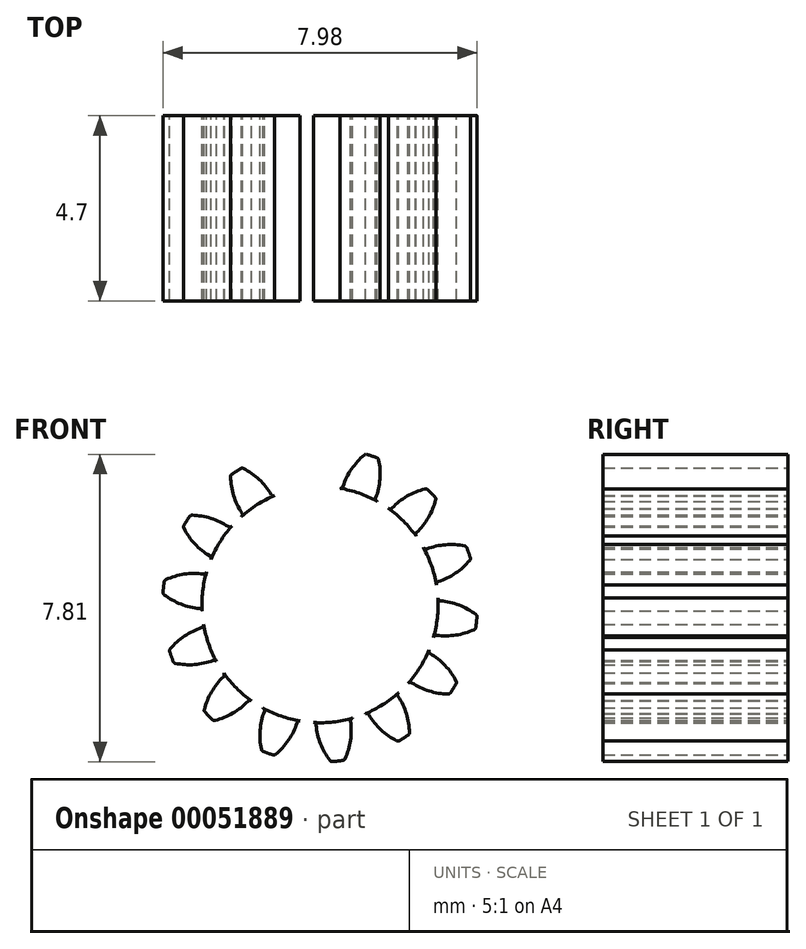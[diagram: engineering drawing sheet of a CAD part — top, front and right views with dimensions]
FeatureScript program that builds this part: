
annotation { "Feature Type Name" : "Feature", "Feature Type Description" : "" }
export const myFeature = defineFeature(function(context is Context, id is Id, definition is map)
    precondition{}
    {
        {
            var Q0;
            Q0=qCreatedBy(makeId("Front.planeOp"),FACE);
            var sketch = newSketch(context, id + "F0", { "sketchPlane" : qUnion([Q0])});
            skCircle(sketch, "E0", {"center": v(0, 0) * mm, "radius": 3 * mm, "construction": true});
            skCircle(sketch, "E1", {"center": v(0, 0) * mm, "radius": 3.5 * mm, "construction": true});
            skCircle(sketch, "E2", {"center": v(0, 0) * mm, "radius": 4 * mm, "construction": true});
            skLineSegment(sketch, "E3", {"start": v(0, 8.23) * mm, "end": v(0, 0) * mm, "construction": true});
            skCircle(sketch, "E4.cCircle", {"center": v(0, 0) * mm, "radius": 8.23 * mm, "construction": true});
            skLineSegment(sketch, "E4.0", {"start": v(0, 8.23) * mm, "end": v(1.83, 8.03) * mm, "construction": true});
            skLineSegment(sketch, "E4.1", {"start": v(1.83, 8.03) * mm, "end": v(3.57, 7.42) * mm, "construction": true});
            skLineSegment(sketch, "E4.2", {"start": v(3.57, 7.42) * mm, "end": v(5.13, 6.44) * mm, "construction": true});
            skLineSegment(sketch, "E4.3", {"start": v(5.13, 6.44) * mm, "end": v(6.44, 5.13) * mm, "construction": true});
            skLineSegment(sketch, "E4.4", {"start": v(6.44, 5.13) * mm, "end": v(7.42, 3.57) * mm, "construction": true});
            skLineSegment(sketch, "E4.5", {"start": v(7.42, 3.57) * mm, "end": v(8.03, 1.83) * mm, "construction": true});
            skLineSegment(sketch, "E4.6", {"start": v(8.03, 1.83) * mm, "end": v(8.23, 0) * mm, "construction": true});
            skLineSegment(sketch, "E4.7", {"start": v(8.23, 0) * mm, "end": v(8.03, -1.83) * mm, "construction": true});
            skLineSegment(sketch, "E4.8", {"start": v(8.03, -1.83) * mm, "end": v(7.42, -3.57) * mm, "construction": true});
            skLineSegment(sketch, "E4.9", {"start": v(7.42, -3.57) * mm, "end": v(6.44, -5.13) * mm, "construction": true});
            skLineSegment(sketch, "E4.10", {"start": v(6.44, -5.13) * mm, "end": v(5.13, -6.44) * mm, "construction": true});
            skLineSegment(sketch, "E4.11", {"start": v(5.13, -6.44) * mm, "end": v(3.57, -7.42) * mm, "construction": true});
            skLineSegment(sketch, "E4.12", {"start": v(3.57, -7.42) * mm, "end": v(1.83, -8.03) * mm, "construction": true});
            skLineSegment(sketch, "E4.13", {"start": v(1.83, -8.03) * mm, "end": v(0, -8.23) * mm, "construction": true});
            skLineSegment(sketch, "E4.14", {"start": v(0, -8.23) * mm, "end": v(-1.83, -8.03) * mm, "construction": true});
            skLineSegment(sketch, "E4.15", {"start": v(-1.83, -8.03) * mm, "end": v(-3.57, -7.42) * mm, "construction": true});
            skLineSegment(sketch, "E4.16", {"start": v(-3.57, -7.42) * mm, "end": v(-5.13, -6.44) * mm, "construction": true});
            skLineSegment(sketch, "E4.17", {"start": v(-5.13, -6.44) * mm, "end": v(-6.44, -5.13) * mm, "construction": true});
            skLineSegment(sketch, "E4.18", {"start": v(-6.44, -5.13) * mm, "end": v(-7.42, -3.57) * mm, "construction": true});
            skLineSegment(sketch, "E4.19", {"start": v(-7.42, -3.57) * mm, "end": v(-8.03, -1.83) * mm, "construction": true});
            skLineSegment(sketch, "E4.20", {"start": v(-8.03, -1.83) * mm, "end": v(-8.23, 0) * mm, "construction": true});
            skLineSegment(sketch, "E4.21", {"start": v(-8.23, 0) * mm, "end": v(-8.03, 1.83) * mm, "construction": true});
            skLineSegment(sketch, "E4.22", {"start": v(-8.03, 1.83) * mm, "end": v(-7.42, 3.57) * mm, "construction": true});
            skLineSegment(sketch, "E4.23", {"start": v(-7.42, 3.57) * mm, "end": v(-6.44, 5.13) * mm, "construction": true});
            skLineSegment(sketch, "E4.24", {"start": v(-6.44, 5.13) * mm, "end": v(-5.13, 6.44) * mm, "construction": true});
            skLineSegment(sketch, "E4.25", {"start": v(-5.13, 6.44) * mm, "end": v(-3.57, 7.42) * mm, "construction": true});
            skLineSegment(sketch, "E4.26", {"start": v(-3.57, 7.42) * mm, "end": v(-1.83, 8.03) * mm, "construction": true});
            skLineSegment(sketch, "E4.27", {"start": v(-1.83, 8.03) * mm, "end": v(0, 8.23) * mm, "construction": true});
            skLineSegment(sketch, "E5.0", {"start": v(-0.93, 8.23) * mm, "end": v(0.93, 8.23) * mm, "construction": true});
            skLineSegment(sketch, "E5.1", {"start": v(0.93, 8.23) * mm, "end": v(2.74, 7.82) * mm, "construction": true});
            skLineSegment(sketch, "E5.2", {"start": v(2.74, 7.82) * mm, "end": v(4.4, 7.02) * mm, "construction": true});
            skLineSegment(sketch, "E5.3", {"start": v(4.4, 7.02) * mm, "end": v(5.86, 5.86) * mm});
            skLineSegment(sketch, "E5.4", {"start": v(5.86, 5.86) * mm, "end": v(7.02, 4.4) * mm});
            skLineSegment(sketch, "E5.5", {"start": v(7.02, 4.4) * mm, "end": v(7.82, 2.74) * mm});
            skLineSegment(sketch, "E5.6", {"start": v(7.82, 2.74) * mm, "end": v(8.23, 0.93) * mm});
            skLineSegment(sketch, "E5.7", {"start": v(8.23, 0.93) * mm, "end": v(8.23, -0.93) * mm});
            skLineSegment(sketch, "E5.8", {"start": v(8.23, -0.93) * mm, "end": v(7.82, -2.74) * mm});
            skLineSegment(sketch, "E5.9", {"start": v(7.82, -2.74) * mm, "end": v(7.02, -4.4) * mm});
            skLineSegment(sketch, "E5.10", {"start": v(7.02, -4.4) * mm, "end": v(5.86, -5.86) * mm});
            skLineSegment(sketch, "E5.11", {"start": v(5.86, -5.86) * mm, "end": v(4.4, -7.02) * mm});
            skLineSegment(sketch, "E5.12", {"start": v(4.4, -7.02) * mm, "end": v(2.74, -7.82) * mm});
            skLineSegment(sketch, "E5.13", {"start": v(2.74, -7.82) * mm, "end": v(0.93, -8.23) * mm});
            skLineSegment(sketch, "E5.14", {"start": v(0.93, -8.23) * mm, "end": v(-0.93, -8.23) * mm});
            skLineSegment(sketch, "E5.15", {"start": v(-0.93, -8.23) * mm, "end": v(-2.74, -7.82) * mm});
            skLineSegment(sketch, "E5.16", {"start": v(-2.74, -7.82) * mm, "end": v(-4.4, -7.02) * mm});
            skLineSegment(sketch, "E5.17", {"start": v(-4.4, -7.02) * mm, "end": v(-5.86, -5.86) * mm});
            skLineSegment(sketch, "E5.18", {"start": v(-5.86, -5.86) * mm, "end": v(-7.02, -4.4) * mm});
            skLineSegment(sketch, "E5.19", {"start": v(-7.02, -4.4) * mm, "end": v(-7.82, -2.74) * mm});
            skLineSegment(sketch, "E5.20", {"start": v(-7.82, -2.74) * mm, "end": v(-8.23, -0.93) * mm});
            skLineSegment(sketch, "E5.21", {"start": v(-8.23, -0.93) * mm, "end": v(-8.23, 0.93) * mm});
            skLineSegment(sketch, "E5.22", {"start": v(-8.23, 0.93) * mm, "end": v(-7.82, 2.74) * mm});
            skLineSegment(sketch, "E5.23", {"start": v(-7.82, 2.74) * mm, "end": v(-7.02, 4.4) * mm});
            skLineSegment(sketch, "E5.24", {"start": v(-7.02, 4.4) * mm, "end": v(-5.86, 5.86) * mm});
            skLineSegment(sketch, "E5.25", {"start": v(-5.86, 5.86) * mm, "end": v(-4.4, 7.02) * mm, "construction": true});
            skLineSegment(sketch, "E5.26", {"start": v(-4.4, 7.02) * mm, "end": v(-2.74, 7.82) * mm, "construction": true});
            skLineSegment(sketch, "E5.27", {"start": v(-2.74, 7.82) * mm, "end": v(-0.93, 8.23) * mm, "construction": true});
            skPoint(sketch, "E5.0.midPoint", {"position": v(0, 8.23) * mm});
            skLineSegment(sketch, "E6", {"start": v(-0.93, 8.23) * mm, "end": v(0, 0) * mm, "construction": true});
            skLineSegment(sketch, "E7", {"start": v(0, 3.5) * mm, "end": v(-9.32, 3.5) * mm, "construction": true});
            skLineSegment(sketch, "E8", {"start": v(0, 3.5) * mm, "end": v(-9.62, 0) * mm, "construction": true});
            skCircle(sketch, "E9", {"center": v(0, 3.5) * mm, "radius": 1.75 * mm, "construction": true});
            skCircle(sketch, "E10", {"center": v(-1.64, 2.9) * mm, "radius": 1.75 * mm, "construction": true});
            skArc(sketch, "E11", {"start": v(-0.25, 3.96) * mm, "mid": v(-0.01, 3.53) * mm, "end": v(0.1, 3.06) * mm});
            skArc(sketch, "E12.MirrorCS", {"start": v(-0.62, 3.95) * mm, "mid": v(-0.78, 3.44) * mm, "end": v(-0.77, 2.9) * mm});
            skArc(sketch, "E13.MirrorCS", {"start": v(-0.64, 3.92) * mm, "mid": v(-0.77, 3.45) * mm, "end": v(-0.78, 2.96) * mm});
            skArc(sketch, "E14", {"start": v(-0.58, 3.96) * mm, "mid": v(-0.45, 3.97) * mm, "end": v(-0.31, 3.99) * mm});
            skArc(sketch, "E15", {"start": v(-0.83, 2.88) * mm, "mid": v(0.34, -2.98) * mm, "end": v(0.16, 3) * mm});
            skPoint(sketch, "E16.visualSharp", {"position": v(-0.77, 2.9) * mm});
            skArc(sketch, "E16.filletArc", {"start": v(-0.83, 2.88) * mm, "mid": v(-0.79, 2.91) * mm, "end": v(-0.78, 2.96) * mm});
            skPoint(sketch, "E17.visualSharp", {"position": v(0.1, 3) * mm});
            skArc(sketch, "E17.filletArc", {"start": v(0.1, 3.06) * mm, "mid": v(0.12, 3.02) * mm, "end": v(0.16, 3) * mm});
            skPoint(sketch, "E18.visualSharp", {"position": v(-0.62, 3.95) * mm});
            skArc(sketch, "E18.filletArc", {"start": v(-0.58, 3.96) * mm, "mid": v(-0.61, 3.94) * mm, "end": v(-0.64, 3.92) * mm});
            skPoint(sketch, "E19.visualSharp", {"position": v(-0.27, 4) * mm});
            skArc(sketch, "E19.filletArc", {"start": v(-0.25, 3.96) * mm, "mid": v(-0.28, 3.98) * mm, "end": v(-0.31, 3.99) * mm});
            skArc(sketch, "E20.1.0", {"start": v(-2.27, 3.25) * mm, "mid": v(-2.2, 2.77) * mm, "end": v(-1.98, 2.33) * mm});
            skArc(sketch, "E20.1.1", {"start": v(-2, 2.24) * mm, "mid": v(-1.97, 2.28) * mm, "end": v(-1.98, 2.33) * mm});
            skArc(sketch, "E20.1.2", {"start": v(-2.24, 3.31) * mm, "mid": v(-2.27, 3.29) * mm, "end": v(-2.27, 3.25) * mm});
            skArc(sketch, "E20.1.3", {"start": v(-2.24, 3.31) * mm, "mid": v(-2.13, 3.39) * mm, "end": v(-2.01, 3.46) * mm});
            skArc(sketch, "E20.1.4", {"start": v(-1.94, 3.46) * mm, "mid": v(-1.55, 3.18) * mm, "end": v(-1.24, 2.8) * mm});
            skArc(sketch, "E20.1.5", {"start": v(-1.94, 3.46) * mm, "mid": v(-1.98, 3.47) * mm, "end": v(-2.01, 3.46) * mm});
            skArc(sketch, "E20.1.6", {"start": v(-1.24, 2.8) * mm, "mid": v(-1.2, 2.77) * mm, "end": v(-1.15, 2.77) * mm});
            skArc(sketch, "E20.2.0", {"start": v(-3.46, 1.94) * mm, "mid": v(-3.18, 1.55) * mm, "end": v(-2.8, 1.24) * mm});
            skArc(sketch, "E20.2.1", {"start": v(-2.77, 1.15) * mm, "mid": v(-2.77, 1.2) * mm, "end": v(-2.8, 1.24) * mm});
            skArc(sketch, "E20.2.2", {"start": v(-3.46, 2.01) * mm, "mid": v(-3.47, 1.98) * mm, "end": v(-3.46, 1.94) * mm});
            skArc(sketch, "E20.2.3", {"start": v(-3.46, 2.01) * mm, "mid": v(-3.39, 2.13) * mm, "end": v(-3.31, 2.24) * mm});
            skArc(sketch, "E20.2.4", {"start": v(-3.25, 2.27) * mm, "mid": v(-2.77, 2.2) * mm, "end": v(-2.33, 1.98) * mm});
            skArc(sketch, "E20.2.5", {"start": v(-3.25, 2.27) * mm, "mid": v(-3.29, 2.27) * mm, "end": v(-3.31, 2.24) * mm});
            skArc(sketch, "E20.2.6", {"start": v(-2.33, 1.98) * mm, "mid": v(-2.28, 1.97) * mm, "end": v(-2.24, 2) * mm});
            skArc(sketch, "E20.3.0", {"start": v(-3.96, 0.25) * mm, "mid": v(-3.53, 0.01) * mm, "end": v(-3.06, -0.1) * mm});
            skArc(sketch, "E20.3.1", {"start": v(-3, -0.16) * mm, "mid": v(-3.02, -0.12) * mm, "end": v(-3.06, -0.1) * mm});
            skArc(sketch, "E20.3.2", {"start": v(-3.99, 0.31) * mm, "mid": v(-3.98, 0.28) * mm, "end": v(-3.96, 0.25) * mm});
            skArc(sketch, "E20.3.3", {"start": v(-3.99, 0.31) * mm, "mid": v(-3.97, 0.45) * mm, "end": v(-3.96, 0.58) * mm});
            skArc(sketch, "E20.3.4", {"start": v(-3.92, 0.64) * mm, "mid": v(-3.45, 0.77) * mm, "end": v(-2.96, 0.78) * mm});
            skArc(sketch, "E20.3.5", {"start": v(-3.92, 0.64) * mm, "mid": v(-3.94, 0.61) * mm, "end": v(-3.96, 0.58) * mm});
            skArc(sketch, "E20.3.6", {"start": v(-2.96, 0.78) * mm, "mid": v(-2.91, 0.79) * mm, "end": v(-2.88, 0.83) * mm});
            skArc(sketch, "E20.4.0", {"start": v(-3.68, -1.5) * mm, "mid": v(-3.19, -1.52) * mm, "end": v(-2.71, -1.42) * mm});
            skArc(sketch, "E20.4.1", {"start": v(-2.63, -1.45) * mm, "mid": v(-2.66, -1.42) * mm, "end": v(-2.71, -1.42) * mm});
            skArc(sketch, "E20.4.2", {"start": v(-3.73, -1.45) * mm, "mid": v(-3.7, -1.48) * mm, "end": v(-3.68, -1.5) * mm});
            skArc(sketch, "E20.4.3", {"start": v(-3.73, -1.45) * mm, "mid": v(-3.78, -1.32) * mm, "end": v(-3.82, -1.2) * mm});
            skArc(sketch, "E20.4.4", {"start": v(-3.8, -1.13) * mm, "mid": v(-3.44, -0.8) * mm, "end": v(-3, -0.58) * mm});
            skArc(sketch, "E20.4.5", {"start": v(-3.8, -1.13) * mm, "mid": v(-3.82, -1.16) * mm, "end": v(-3.82, -1.2) * mm});
            skArc(sketch, "E20.4.6", {"start": v(-3, -0.58) * mm, "mid": v(-2.97, -0.55) * mm, "end": v(-2.96, -0.5) * mm});
            skArc(sketch, "E20.5.0", {"start": v(-2.67, -2.94) * mm, "mid": v(-2.21, -2.76) * mm, "end": v(-1.83, -2.45) * mm});
            skArc(sketch, "E20.5.1", {"start": v(-1.74, -2.44) * mm, "mid": v(-1.79, -2.43) * mm, "end": v(-1.83, -2.45) * mm});
            skArc(sketch, "E20.5.2", {"start": v(-2.73, -2.92) * mm, "mid": v(-2.7, -2.94) * mm, "end": v(-2.67, -2.94) * mm});
            skArc(sketch, "E20.5.3", {"start": v(-2.73, -2.92) * mm, "mid": v(-2.83, -2.83) * mm, "end": v(-2.92, -2.73) * mm});
            skArc(sketch, "E20.5.4", {"start": v(-2.94, -2.67) * mm, "mid": v(-2.76, -2.21) * mm, "end": v(-2.45, -1.83) * mm});
            skArc(sketch, "E20.5.5", {"start": v(-2.94, -2.67) * mm, "mid": v(-2.94, -2.7) * mm, "end": v(-2.92, -2.73) * mm});
            skArc(sketch, "E20.5.6", {"start": v(-2.45, -1.83) * mm, "mid": v(-2.43, -1.79) * mm, "end": v(-2.44, -1.74) * mm});
            skArc(sketch, "E20.6.0", {"start": v(-1.13, -3.8) * mm, "mid": v(-0.8, -3.44) * mm, "end": v(-0.58, -3) * mm});
            skArc(sketch, "E20.6.1", {"start": v(-0.5, -2.96) * mm, "mid": v(-0.55, -2.97) * mm, "end": v(-0.58, -3) * mm});
            skArc(sketch, "E20.6.2", {"start": v(-1.2, -3.82) * mm, "mid": v(-1.16, -3.82) * mm, "end": v(-1.13, -3.8) * mm});
            skArc(sketch, "E20.6.3", {"start": v(-1.2, -3.82) * mm, "mid": v(-1.32, -3.78) * mm, "end": v(-1.45, -3.73) * mm});
            skArc(sketch, "E20.6.4", {"start": v(-1.5, -3.68) * mm, "mid": v(-1.52, -3.19) * mm, "end": v(-1.42, -2.71) * mm});
            skArc(sketch, "E20.6.5", {"start": v(-1.5, -3.68) * mm, "mid": v(-1.48, -3.7) * mm, "end": v(-1.45, -3.73) * mm});
            skArc(sketch, "E20.6.6", {"start": v(-1.42, -2.71) * mm, "mid": v(-1.42, -2.66) * mm, "end": v(-1.45, -2.63) * mm});
            skArc(sketch, "E20.7.0", {"start": v(0.64, -3.92) * mm, "mid": v(0.77, -3.45) * mm, "end": v(0.78, -2.96) * mm});
            skArc(sketch, "E20.7.1", {"start": v(0.83, -2.88) * mm, "mid": v(0.79, -2.91) * mm, "end": v(0.78, -2.96) * mm});
            skArc(sketch, "E20.7.2", {"start": v(0.58, -3.96) * mm, "mid": v(0.61, -3.94) * mm, "end": v(0.64, -3.92) * mm});
            skArc(sketch, "E20.7.3", {"start": v(0.58, -3.96) * mm, "mid": v(0.45, -3.97) * mm, "end": v(0.31, -3.99) * mm});
            skArc(sketch, "E20.7.4", {"start": v(0.25, -3.96) * mm, "mid": v(0.01, -3.53) * mm, "end": v(-0.1, -3.06) * mm});
            skArc(sketch, "E20.7.5", {"start": v(0.25, -3.96) * mm, "mid": v(0.28, -3.98) * mm, "end": v(0.31, -3.99) * mm});
            skArc(sketch, "E20.7.6", {"start": v(-0.1, -3.06) * mm, "mid": v(-0.12, -3.02) * mm, "end": v(-0.16, -3) * mm});
            skArc(sketch, "E20.8.0", {"start": v(2.27, -3.25) * mm, "mid": v(2.2, -2.77) * mm, "end": v(1.98, -2.33) * mm});
            skArc(sketch, "E20.8.1", {"start": v(2, -2.24) * mm, "mid": v(1.97, -2.28) * mm, "end": v(1.98, -2.33) * mm});
            skArc(sketch, "E20.8.2", {"start": v(2.24, -3.31) * mm, "mid": v(2.27, -3.29) * mm, "end": v(2.27, -3.25) * mm});
            skArc(sketch, "E20.8.3", {"start": v(2.24, -3.31) * mm, "mid": v(2.13, -3.39) * mm, "end": v(2.01, -3.46) * mm});
            skArc(sketch, "E20.8.4", {"start": v(1.94, -3.46) * mm, "mid": v(1.55, -3.18) * mm, "end": v(1.24, -2.8) * mm});
            skArc(sketch, "E20.8.5", {"start": v(1.94, -3.46) * mm, "mid": v(1.98, -3.47) * mm, "end": v(2.01, -3.46) * mm});
            skArc(sketch, "E20.8.6", {"start": v(1.24, -2.8) * mm, "mid": v(1.2, -2.77) * mm, "end": v(1.15, -2.77) * mm});
            skArc(sketch, "E20.9.0", {"start": v(3.46, -1.94) * mm, "mid": v(3.18, -1.55) * mm, "end": v(2.8, -1.24) * mm});
            skArc(sketch, "E20.9.1", {"start": v(2.77, -1.15) * mm, "mid": v(2.77, -1.2) * mm, "end": v(2.8, -1.24) * mm});
            skArc(sketch, "E20.9.2", {"start": v(3.46, -2.01) * mm, "mid": v(3.47, -1.98) * mm, "end": v(3.46, -1.94) * mm});
            skArc(sketch, "E20.9.3", {"start": v(3.46, -2.01) * mm, "mid": v(3.39, -2.13) * mm, "end": v(3.31, -2.24) * mm});
            skArc(sketch, "E20.9.4", {"start": v(3.25, -2.27) * mm, "mid": v(2.77, -2.2) * mm, "end": v(2.33, -1.98) * mm});
            skArc(sketch, "E20.9.5", {"start": v(3.25, -2.27) * mm, "mid": v(3.29, -2.27) * mm, "end": v(3.31, -2.24) * mm});
            skArc(sketch, "E20.9.6", {"start": v(2.33, -1.98) * mm, "mid": v(2.28, -1.97) * mm, "end": v(2.24, -2) * mm});
            skArc(sketch, "E20.10.0", {"start": v(3.96, -0.25) * mm, "mid": v(3.53, -0.01) * mm, "end": v(3.06, 0.1) * mm});
            skArc(sketch, "E20.10.1", {"start": v(3, 0.16) * mm, "mid": v(3.02, 0.12) * mm, "end": v(3.06, 0.1) * mm});
            skArc(sketch, "E20.10.2", {"start": v(3.99, -0.31) * mm, "mid": v(3.98, -0.28) * mm, "end": v(3.96, -0.25) * mm});
            skArc(sketch, "E20.10.3", {"start": v(3.99, -0.31) * mm, "mid": v(3.97, -0.45) * mm, "end": v(3.96, -0.58) * mm});
            skArc(sketch, "E20.10.4", {"start": v(3.92, -0.64) * mm, "mid": v(3.45, -0.77) * mm, "end": v(2.96, -0.78) * mm});
            skArc(sketch, "E20.10.5", {"start": v(3.92, -0.64) * mm, "mid": v(3.94, -0.61) * mm, "end": v(3.96, -0.58) * mm});
            skArc(sketch, "E20.10.6", {"start": v(2.96, -0.78) * mm, "mid": v(2.91, -0.79) * mm, "end": v(2.88, -0.83) * mm});
            skArc(sketch, "E20.11.0", {"start": v(3.68, 1.5) * mm, "mid": v(3.19, 1.52) * mm, "end": v(2.71, 1.42) * mm});
            skArc(sketch, "E20.11.1", {"start": v(2.63, 1.45) * mm, "mid": v(2.66, 1.42) * mm, "end": v(2.71, 1.42) * mm});
            skArc(sketch, "E20.11.2", {"start": v(3.73, 1.45) * mm, "mid": v(3.7, 1.48) * mm, "end": v(3.68, 1.5) * mm});
            skArc(sketch, "E20.11.3", {"start": v(3.73, 1.45) * mm, "mid": v(3.78, 1.32) * mm, "end": v(3.82, 1.2) * mm});
            skArc(sketch, "E20.11.4", {"start": v(3.8, 1.13) * mm, "mid": v(3.44, 0.8) * mm, "end": v(3, 0.58) * mm});
            skArc(sketch, "E20.11.5", {"start": v(3.8, 1.13) * mm, "mid": v(3.82, 1.16) * mm, "end": v(3.82, 1.2) * mm});
            skArc(sketch, "E20.11.6", {"start": v(3, 0.58) * mm, "mid": v(2.97, 0.55) * mm, "end": v(2.96, 0.5) * mm});
            skArc(sketch, "E20.12.0", {"start": v(2.67, 2.94) * mm, "mid": v(2.21, 2.76) * mm, "end": v(1.83, 2.45) * mm});
            skArc(sketch, "E20.12.1", {"start": v(1.74, 2.44) * mm, "mid": v(1.79, 2.43) * mm, "end": v(1.83, 2.45) * mm});
            skArc(sketch, "E20.12.2", {"start": v(2.73, 2.92) * mm, "mid": v(2.7, 2.94) * mm, "end": v(2.67, 2.94) * mm});
            skArc(sketch, "E20.12.3", {"start": v(2.73, 2.92) * mm, "mid": v(2.83, 2.83) * mm, "end": v(2.92, 2.73) * mm});
            skArc(sketch, "E20.12.4", {"start": v(2.94, 2.67) * mm, "mid": v(2.76, 2.21) * mm, "end": v(2.45, 1.83) * mm});
            skArc(sketch, "E20.12.5", {"start": v(2.94, 2.67) * mm, "mid": v(2.94, 2.7) * mm, "end": v(2.92, 2.73) * mm});
            skArc(sketch, "E20.12.6", {"start": v(2.45, 1.83) * mm, "mid": v(2.43, 1.79) * mm, "end": v(2.44, 1.74) * mm});
            skArc(sketch, "E20.13.0", {"start": v(1.13, 3.8) * mm, "mid": v(0.8, 3.44) * mm, "end": v(0.58, 3) * mm});
            skArc(sketch, "E20.13.1", {"start": v(0.5, 2.96) * mm, "mid": v(0.55, 2.97) * mm, "end": v(0.58, 3) * mm});
            skArc(sketch, "E20.13.2", {"start": v(1.2, 3.82) * mm, "mid": v(1.16, 3.82) * mm, "end": v(1.13, 3.8) * mm});
            skArc(sketch, "E20.13.3", {"start": v(1.2, 3.82) * mm, "mid": v(1.32, 3.78) * mm, "end": v(1.45, 3.73) * mm});
            skArc(sketch, "E20.13.4", {"start": v(1.5, 3.68) * mm, "mid": v(1.52, 3.19) * mm, "end": v(1.42, 2.71) * mm});
            skArc(sketch, "E20.13.5", {"start": v(1.5, 3.68) * mm, "mid": v(1.48, 3.7) * mm, "end": v(1.45, 3.73) * mm});
            skArc(sketch, "E20.13.6", {"start": v(1.42, 2.71) * mm, "mid": v(1.42, 2.66) * mm, "end": v(1.45, 2.63) * mm});
            skSolve(sketch);
        }
        {
            var Q0;
            Q0=makeQuery(id+"F0.imprint","IMPRINT",FACE,{"disambiguationData":[TD([[makeQuery(id+"F0.imprint","IMPRINT",EDGE,{"derivedFrom":sQuery(id+"F0.wireOp",EDGE,"E11")}),-1.0]])]});
            var Q1;
            Q1=makeQuery(id+"F0.imprint","IMPRINT",FACE,{"disambiguationData":[TD([[makeQuery(id+"F0.imprint","IMPRINT",EDGE,{"derivedFrom":sQuery(id+"F0.wireOp",EDGE,"E20.1.0")}),1.0]])]});
            var Q2;
            Q2=makeQuery(id+"F0.imprint","IMPRINT",FACE,{"disambiguationData":[TD([[makeQuery(id+"F0.imprint","IMPRINT",EDGE,{"derivedFrom":sQuery(id+"F0.wireOp",EDGE,"E20.3.0")}),1.0]])]});
            var Q3;
            Q3=makeQuery(id+"F0.imprint","IMPRINT",FACE,{"disambiguationData":[TD([[makeQuery(id+"F0.imprint","IMPRINT",EDGE,{"derivedFrom":sQuery(id+"F0.wireOp",EDGE,"E20.5.0")}),1.0]])]});
            var Q4;
            Q4=makeQuery(id+"F0.imprint","IMPRINT",FACE,{"disambiguationData":[TD([[makeQuery(id+"F0.imprint","IMPRINT",EDGE,{"derivedFrom":sQuery(id+"F0.wireOp",EDGE,"E20.6.0")}),1.0]])]});
            var Q5;
            Q5=makeQuery(id+"F0.imprint","IMPRINT",FACE,{"disambiguationData":[TD([[makeQuery(id+"F0.imprint","IMPRINT",EDGE,{"derivedFrom":sQuery(id+"F0.wireOp",EDGE,"E20.7.0")}),1.0]])]});
            var Q6;
            Q6=makeQuery(id+"F0.imprint","IMPRINT",FACE,{"disambiguationData":[TD([[makeQuery(id+"F0.imprint","IMPRINT",EDGE,{"derivedFrom":sQuery(id+"F0.wireOp",EDGE,"E20.8.0")}),1.0]])]});
            var Q7;
            Q7=makeQuery(id+"F0.imprint","IMPRINT",FACE,{"disambiguationData":[TD([[makeQuery(id+"F0.imprint","IMPRINT",EDGE,{"derivedFrom":sQuery(id+"F0.wireOp",EDGE,"E20.9.0")}),1.0]])]});
            var Q8;
            Q8=makeQuery(id+"F0.imprint","IMPRINT",FACE,{"disambiguationData":[TD([[makeQuery(id+"F0.imprint","IMPRINT",EDGE,{"derivedFrom":sQuery(id+"F0.wireOp",EDGE,"E20.10.0")}),1.0]])]});
            var Q9;
            Q9=makeQuery(id+"F0.imprint","IMPRINT",FACE,{"disambiguationData":[TD([[makeQuery(id+"F0.imprint","IMPRINT",EDGE,{"derivedFrom":sQuery(id+"F0.wireOp",EDGE,"E20.11.0")}),1.0]])]});
            var Q10;
            Q10=makeQuery(id+"F0.imprint","IMPRINT",FACE,{"disambiguationData":[TD([[makeQuery(id+"F0.imprint","IMPRINT",EDGE,{"derivedFrom":sQuery(id+"F0.wireOp",EDGE,"E20.12.0")}),1.0]])]});
            var Q11;
            Q11=makeQuery(id+"F0.imprint","IMPRINT",FACE,{"disambiguationData":[TD([[makeQuery(id+"F0.imprint","IMPRINT",EDGE,{"derivedFrom":sQuery(id+"F0.wireOp",EDGE,"E20.13.0")}),1.0]])]});
            var Q12;
            Q12=makeQuery(id+"F0.imprint","IMPRINT",FACE,{"disambiguationData":[TD([[makeQuery(id+"F0.imprint","IMPRINT",EDGE,{"derivedFrom":sQuery(id+"F0.wireOp",EDGE,"E20.2.0")}),1.0]])]});
            var Q13;
            Q13=makeQuery(id+"F0.imprint","IMPRINT",FACE,{"disambiguationData":[TD([[makeQuery(id+"F0.imprint","IMPRINT",EDGE,{"derivedFrom":sQuery(id+"F0.wireOp",EDGE,"E20.4.0")}),1.0]])]});
            extrude(context, id + "F1", {"entities" : qUnion([Q0, Q1, Q2, Q3, Q4, Q5, Q6, Q7, Q8, Q9, Q10, Q11, Q12, Q13]), "depth" : 4.7 * mm});
        }
        {
            var Q0;
            Q0=makeQuery(id+"F1.opExtrude","CAP_FACE",FACE,{"disambiguationData":[OSD([sQuery(id+"F0.wireOp",EDGE,"E11"),sQuery(id+"F0.wireOp",EDGE,"E13.MirrorCS"),sQuery(id+"F0.wireOp",EDGE,"E14"),sQuery(id+"F0.wireOp",EDGE,"E15"),sQuery(id+"F0.wireOp",EDGE,"E16.filletArc"),sQuery(id+"F0.wireOp",EDGE,"E17.filletArc"),sQuery(id+"F0.wireOp",EDGE,"E18.filletArc"),sQuery(id+"F0.wireOp",EDGE,"E19.filletArc"),sQuery(id+"F0.wireOp",EDGE,"E20.1.0"),sQuery(id+"F0.wireOp",EDGE,"E20.1.1"),sQuery(id+"F0.wireOp",EDGE,"E20.1.2"),sQuery(id+"F0.wireOp",EDGE,"E20.1.3"),sQuery(id+"F0.wireOp",EDGE,"E20.1.4"),sQuery(id+"F0.wireOp",EDGE,"E20.1.5"),sQuery(id+"F0.wireOp",EDGE,"E20.1.6"),sQuery(id+"F0.wireOp",EDGE,"E20.2.0"),sQuery(id+"F0.wireOp",EDGE,"E20.2.1"),sQuery(id+"F0.wireOp",EDGE,"E20.2.2"),sQuery(id+"F0.wireOp",EDGE,"E20.2.3"),sQuery(id+"F0.wireOp",EDGE,"E20.2.4"),sQuery(id+"F0.wireOp",EDGE,"E20.2.5"),sQuery(id+"F0.wireOp",EDGE,"E20.2.6"),sQuery(id+"F0.wireOp",EDGE,"E20.3.0"),sQuery(id+"F0.wireOp",EDGE,"E20.3.1"),sQuery(id+"F0.wireOp",EDGE,"E20.3.2"),sQuery(id+"F0.wireOp",EDGE,"E20.3.3"),sQuery(id+"F0.wireOp",EDGE,"E20.3.4"),sQuery(id+"F0.wireOp",EDGE,"E20.3.5"),sQuery(id+"F0.wireOp",EDGE,"E20.3.6"),sQuery(id+"F0.wireOp",EDGE,"E20.4.0"),sQuery(id+"F0.wireOp",EDGE,"E20.4.1"),sQuery(id+"F0.wireOp",EDGE,"E20.4.2"),sQuery(id+"F0.wireOp",EDGE,"E20.4.3"),sQuery(id+"F0.wireOp",EDGE,"E20.4.4"),sQuery(id+"F0.wireOp",EDGE,"E20.4.5"),sQuery(id+"F0.wireOp",EDGE,"E20.4.6"),sQuery(id+"F0.wireOp",EDGE,"E20.5.0"),sQuery(id+"F0.wireOp",EDGE,"E20.5.1"),sQuery(id+"F0.wireOp",EDGE,"E20.5.2"),sQuery(id+"F0.wireOp",EDGE,"E20.5.3"),sQuery(id+"F0.wireOp",EDGE,"E20.5.4"),sQuery(id+"F0.wireOp",EDGE,"E20.5.5"),sQuery(id+"F0.wireOp",EDGE,"E20.5.6"),sQuery(id+"F0.wireOp",EDGE,"E20.6.0"),sQuery(id+"F0.wireOp",EDGE,"E20.6.1"),sQuery(id+"F0.wireOp",EDGE,"E20.6.2"),sQuery(id+"F0.wireOp",EDGE,"E20.6.3"),sQuery(id+"F0.wireOp",EDGE,"E20.6.4"),sQuery(id+"F0.wireOp",EDGE,"E20.6.5"),sQuery(id+"F0.wireOp",EDGE,"E20.6.6"),sQuery(id+"F0.wireOp",EDGE,"E20.7.0"),sQuery(id+"F0.wireOp",EDGE,"E20.7.1"),sQuery(id+"F0.wireOp",EDGE,"E20.7.2"),sQuery(id+"F0.wireOp",EDGE,"E20.7.3"),sQuery(id+"F0.wireOp",EDGE,"E20.7.4"),sQuery(id+"F0.wireOp",EDGE,"E20.7.5"),sQuery(id+"F0.wireOp",EDGE,"E20.7.6"),sQuery(id+"F0.wireOp",EDGE,"E20.8.0"),sQuery(id+"F0.wireOp",EDGE,"E20.8.1"),sQuery(id+"F0.wireOp",EDGE,"E20.8.2"),sQuery(id+"F0.wireOp",EDGE,"E20.8.3"),sQuery(id+"F0.wireOp",EDGE,"E20.8.4"),sQuery(id+"F0.wireOp",EDGE,"E20.8.5"),sQuery(id+"F0.wireOp",EDGE,"E20.8.6"),sQuery(id+"F0.wireOp",EDGE,"E20.9.0"),sQuery(id+"F0.wireOp",EDGE,"E20.9.1"),sQuery(id+"F0.wireOp",EDGE,"E20.9.2"),sQuery(id+"F0.wireOp",EDGE,"E20.9.3"),sQuery(id+"F0.wireOp",EDGE,"E20.9.4"),sQuery(id+"F0.wireOp",EDGE,"E20.9.5"),sQuery(id+"F0.wireOp",EDGE,"E20.9.6"),sQuery(id+"F0.wireOp",EDGE,"E20.10.0"),sQuery(id+"F0.wireOp",EDGE,"E20.10.1"),sQuery(id+"F0.wireOp",EDGE,"E20.10.2"),sQuery(id+"F0.wireOp",EDGE,"E20.10.3"),sQuery(id+"F0.wireOp",EDGE,"E20.10.4"),sQuery(id+"F0.wireOp",EDGE,"E20.10.5"),sQuery(id+"F0.wireOp",EDGE,"E20.10.6"),sQuery(id+"F0.wireOp",EDGE,"E20.11.0"),sQuery(id+"F0.wireOp",EDGE,"E20.11.1"),sQuery(id+"F0.wireOp",EDGE,"E20.11.2"),sQuery(id+"F0.wireOp",EDGE,"E20.11.3"),sQuery(id+"F0.wireOp",EDGE,"E20.11.4"),sQuery(id+"F0.wireOp",EDGE,"E20.11.5"),sQuery(id+"F0.wireOp",EDGE,"E20.11.6"),sQuery(id+"F0.wireOp",EDGE,"E20.12.0"),sQuery(id+"F0.wireOp",EDGE,"E20.12.1"),sQuery(id+"F0.wireOp",EDGE,"E20.12.2"),sQuery(id+"F0.wireOp",EDGE,"E20.12.3"),sQuery(id+"F0.wireOp",EDGE,"E20.12.4"),sQuery(id+"F0.wireOp",EDGE,"E20.12.5"),sQuery(id+"F0.wireOp",EDGE,"E20.12.6"),sQuery(id+"F0.wireOp",EDGE,"E20.13.0"),sQuery(id+"F0.wireOp",EDGE,"E20.13.1"),sQuery(id+"F0.wireOp",EDGE,"E20.13.2"),sQuery(id+"F0.wireOp",EDGE,"E20.13.3"),sQuery(id+"F0.wireOp",EDGE,"E20.13.4"),sQuery(id+"F0.wireOp",EDGE,"E20.13.5"),sQuery(id+"F0.wireOp",EDGE,"E20.13.6")])],"isStart":false});
            var sketch = newSketch(context, id + "F2", { "sketchPlane" : qUnion([Q0])});
            skCircle(sketch, "E21", {"center": v(0, 0) * mm, "radius": 1 * mm});
            skSolve(sketch);
        }
        {
            var Q0;
            Q0 = qSketchRegion(id + "F2", true);
            extrude(context, id + "F3", {"entities" : qUnion([Q0]), "operationType" : NewBodyOperationType.REMOVE, "endBound" : BoundingType.THROUGH_ALL, "oppositeDirection" : true, "depth" : 25 * mm});
        }
    });
